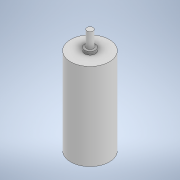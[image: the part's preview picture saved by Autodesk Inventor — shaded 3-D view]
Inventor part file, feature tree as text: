
AUTODESK INVENTOR PART (.ipt)
format: ipt  version: 2020 (Build 240168000, 168)  size: 105,984 bytes
history: native  units: mm
features: extrude x3, sketch x3, other x1
ambient origin geometry x8: Origin, YZ Plane, XZ Plane, XY Plane, X Axis, Y Axis, Z Axis, Center Point
bodies: Body1 (feature_tree)
feature tree (7):
  other  "Bryła1"
  extrude  "Wyciągnięcie proste1"  Depth=25.0mm
  extrude  "Wyciągnięcie proste2"  Depth=56.0mm TaperAngle=0.0deg
  extrude  "Wyciągnięcie proste3"  Depth=4.0mm
  sketch  "Szkic1"
  sketch  "Szkic2"
  sketch  "Szkic3"
